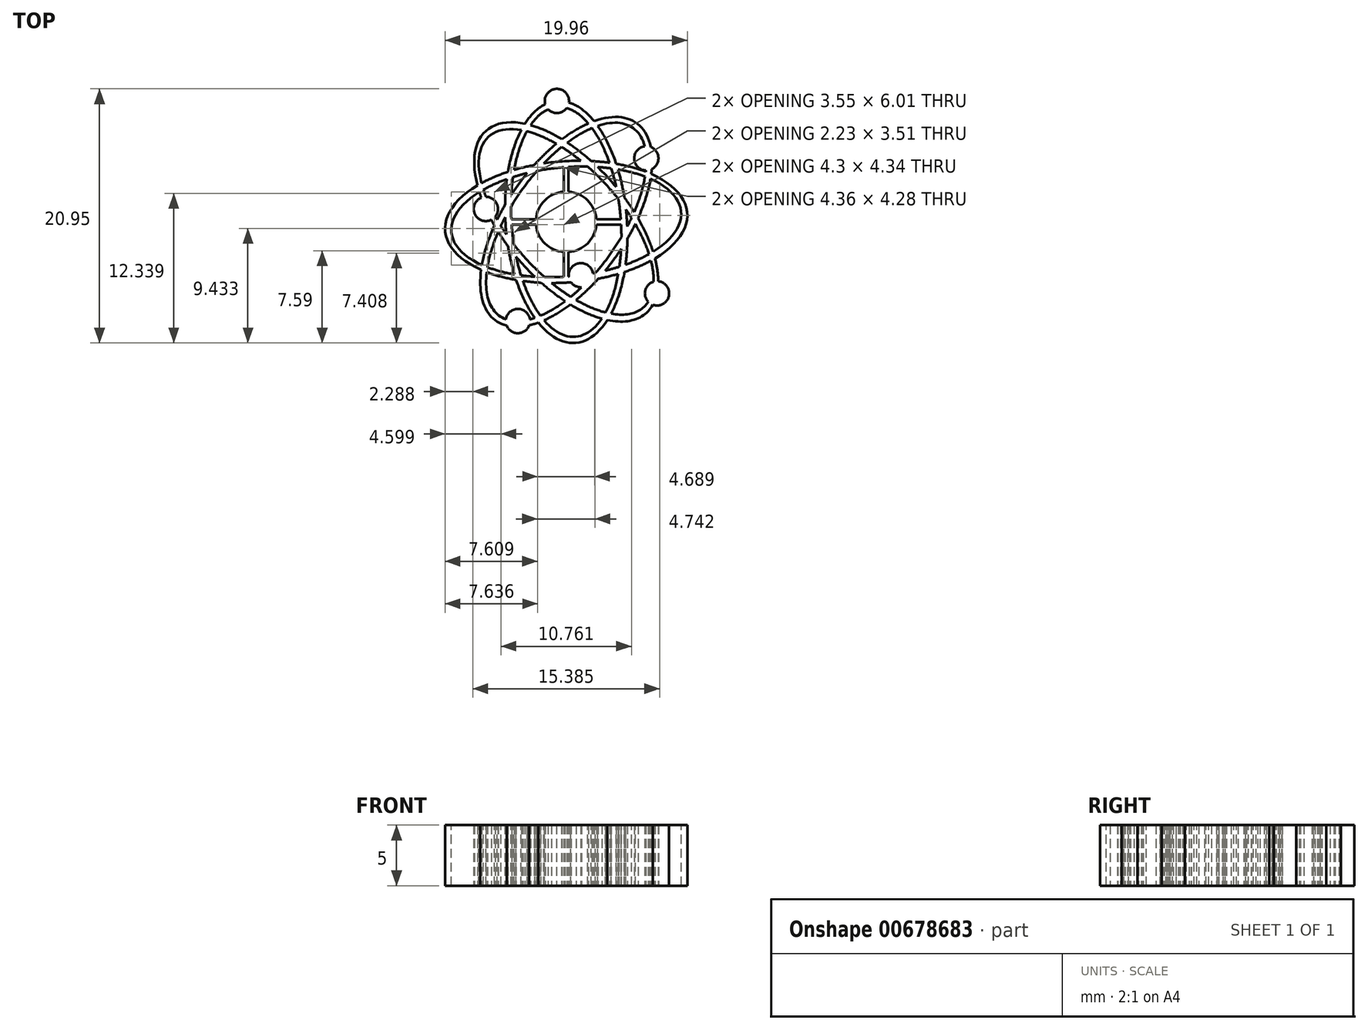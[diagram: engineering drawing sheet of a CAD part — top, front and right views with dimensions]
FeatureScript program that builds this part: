
annotation { "Feature Type Name" : "Feature", "Feature Type Description" : "" }
export const myFeature = defineFeature(function(context is Context, id is Id, definition is map)
    precondition{}
    {
        {
            var Q0;
            Q0=qCreatedBy(makeId("Top.planeOp"),FACE);
            var sketch = newSketch(context, id + "F0", { "sketchPlane" : qUnion([Q0])});
            skCircle(sketch, "E0", {"center": v(0, 0) * mm, "radius": 2.5 * mm});
            skEllipse(sketch, "E1", {"center": v(0, 0) * mm, "majorRadius": 10 * mm, "minorRadius": 5 * mm, "majorAxis": v(-0.66, 0.75)});
            skEllipse(sketch, "E2", {"center": v(0, 0) * mm, "majorRadius": 10 * mm, "minorRadius": 5 * mm, "majorAxis": v(0.58, 0.82)});
            skEllipse(sketch, "E3", {"center": v(0, 0) * mm, "majorRadius": 10 * mm, "minorRadius": 5 * mm, "majorAxis": v(-1, -0.07)});
            skEllipse(sketch, "E4", {"center": v(0, 0) * mm, "majorRadius": 9.5 * mm, "minorRadius": 4.5 * mm, "majorAxis": v(-0.67, 0.74)});
            skEllipse(sketch, "E5", {"center": v(0, 0) * mm, "majorRadius": 9.5 * mm, "minorRadius": 4.5 * mm, "majorAxis": v(-1, -0.09)});
            skEllipse(sketch, "E6", {"center": v(0, 0) * mm, "majorRadius": 9.5 * mm, "minorRadius": 4.5 * mm, "majorAxis": v(0.58, 0.82)});
            skEllipse(sketch, "E7", {"center": v(0, 0) * mm, "majorRadius": 10 * mm, "minorRadius": 5 * mm, "majorAxis": v(-0.08, 1)});
            skEllipse(sketch, "E8", {"center": v(0, 0) * mm, "majorRadius": 9.5 * mm, "minorRadius": 4.5 * mm, "majorAxis": v(-0.08, 1)});
            skCircle(sketch, "E9", {"center": v(-0.77, 9.97) * mm, "radius": 1 * mm});
            skCircle(sketch, "E10", {"center": v(-6.62, 1.07) * mm, "radius": 1 * mm});
            skCircle(sketch, "E11", {"center": v(6.6, 5.24) * mm, "radius": 1 * mm});
            skCircle(sketch, "E12", {"center": v(1.2, -4.4) * mm, "radius": 1 * mm});
            skCircle(sketch, "E13", {"center": v(7.48, -5.9) * mm, "radius": 1 * mm});
            skCircle(sketch, "E14", {"center": v(-3.98, -8.18) * mm, "radius": 1 * mm});
            skLineSegment(sketch, "E15.bottom", {"start": v(0.2, 4.78) * mm, "end": v(-0.2, 4.78) * mm});
            skLineSegment(sketch, "E15.top", {"start": v(0.2, -4.78) * mm, "end": v(-0.2, -4.78) * mm});
            skLineSegment(sketch, "E15.left", {"start": v(0.2, 4.78) * mm, "end": v(0.2, -4.78) * mm});
            skLineSegment(sketch, "E15.right", {"start": v(-0.2, 4.78) * mm, "end": v(-0.2, -4.78) * mm});
            skLineSegment(sketch, "E16.bottom", {"start": v(-4.84, -0.22) * mm, "end": v(4.84, -0.22) * mm});
            skLineSegment(sketch, "E16.top", {"start": v(-4.84, 0.22) * mm, "end": v(4.84, 0.22) * mm});
            skLineSegment(sketch, "E16.left", {"start": v(-4.84, -0.22) * mm, "end": v(-4.84, 0.22) * mm});
            skLineSegment(sketch, "E16.right", {"start": v(4.84, -0.22) * mm, "end": v(4.84, 0.22) * mm});
            skSolve(sketch);
        }
        {
            var Q0;
            Q0 = qSketchRegion(id + "F0", true);
            var Q1;
            {var subQ0=sQuery(id+"F0.wireOp",EDGE,"dH836gxZ-2VDt-7VUX-VpBF-xnlLIh1VEINP");var subQ1=sQuery(id+"F0.wireOp",EDGE,"E1");var subQ2=makeQuery(id+"F0.imprint","INTERSECT",VERTEX,{"disambiguationData":[OD(0.0)],"derivedFrom":[subQ1,subQ0]});Q1=makeQuery(id+"F0.imprint","IMPRINT",FACE,{"disambiguationData":[TD([[makeQuery(id+"F0.imprint","IMPRINT",EDGE,{"disambiguationData":[TD([[subQ2,-1.0]])],"derivedFrom":subQ1}),-1.0]])]});}
            var Q2;
            {var subQ0=sQuery(id+"F0.wireOp",EDGE,"dH836gxZ-2VDt-7VUX-VpBF-xnlLIh1VEINP");var subQ1=sQuery(id+"F0.wireOp",EDGE,"E1");var subQ2=makeQuery(id+"F0.imprint","INTERSECT",VERTEX,{"disambiguationData":[OD(0.0)],"derivedFrom":[subQ1,subQ0]});Q2=makeQuery(id+"F0.imprint","IMPRINT",FACE,{"disambiguationData":[TD([[makeQuery(id+"F0.imprint","IMPRINT",EDGE,{"disambiguationData":[TD([[subQ2,-1.0]])],"derivedFrom":subQ1}),1.0]])]});}
            var Q3;
            {var subQ0=sQuery(id+"F0.wireOp",EDGE,"dH836gxZ-2VDt-7VUX-VpBF-xnlLIh1VEINP");var subQ1=sQuery(id+"F0.wireOp",EDGE,"E4");var subQ2=makeQuery(id+"F0.imprint","INTERSECT",VERTEX,{"disambiguationData":[OD(0.0)],"derivedFrom":[subQ1,subQ0]});Q3=makeQuery(id+"F0.imprint","IMPRINT",FACE,{"disambiguationData":[TD([[makeQuery(id+"F0.imprint","IMPRINT",EDGE,{"disambiguationData":[TD([[subQ2,-1.0]])],"derivedFrom":subQ1}),1.0]])]});}
            var Q4;
            {var subQ0=sQuery(id+"F0.wireOp",EDGE,"E7");var subQ1=sQuery(id+"F0.wireOp",EDGE,"E3");var subQ2=makeQuery(id+"F0.imprint","INTERSECT",VERTEX,{"disambiguationData":[OD(1.0)],"derivedFrom":[subQ1,subQ0]});Q4=makeQuery(id+"F0.imprint","IMPRINT",FACE,{"disambiguationData":[TD([[makeQuery(id+"F0.imprint","IMPRINT",EDGE,{"disambiguationData":[TD([[subQ2,-1.0]])],"derivedFrom":subQ1}),1.0]])]});}
            var Q5;
            {var subQ0=sQuery(id+"F0.wireOp",EDGE,"E2");var subQ1=sQuery(id+"F0.wireOp",EDGE,"E1");var subQ2=makeQuery(id+"F0.imprint","INTERSECT",VERTEX,{"disambiguationData":[OD(2.0)],"derivedFrom":[subQ1,subQ0]});Q5=makeQuery(id+"F0.imprint","IMPRINT",FACE,{"disambiguationData":[TD([[makeQuery(id+"F0.imprint","IMPRINT",EDGE,{"disambiguationData":[TD([[subQ2,-1.0]])],"derivedFrom":subQ1}),-1.0]])]});}
            var Q6;
            {var subQ0=sQuery(id+"F0.wireOp",EDGE,"E2");var subQ1=sQuery(id+"F0.wireOp",EDGE,"E1");var subQ2=makeQuery(id+"F0.imprint","INTERSECT",VERTEX,{"disambiguationData":[OD(2.0)],"derivedFrom":[subQ1,subQ0]});Q6=makeQuery(id+"F0.imprint","IMPRINT",FACE,{"disambiguationData":[TD([[makeQuery(id+"F0.imprint","IMPRINT",EDGE,{"disambiguationData":[TD([[subQ2,-1.0]])],"derivedFrom":subQ1}),1.0]])]});}
            var Q7;
            {var subQ0=sQuery(id+"F0.wireOp",EDGE,"E6");var subQ1=sQuery(id+"F0.wireOp",EDGE,"E1");var subQ2=makeQuery(id+"F0.imprint","INTERSECT",VERTEX,{"disambiguationData":[OD(2.0)],"derivedFrom":[subQ1,subQ0]});Q7=makeQuery(id+"F0.imprint","IMPRINT",FACE,{"disambiguationData":[TD([[makeQuery(id+"F0.imprint","IMPRINT",EDGE,{"disambiguationData":[TD([[subQ2,-1.0]])],"derivedFrom":subQ1}),1.0]])]});}
            var Q8;
            {var subQ0=sQuery(id+"F0.wireOp",EDGE,"E7");var subQ1=sQuery(id+"F0.wireOp",EDGE,"E1");var subQ2=makeQuery(id+"F0.imprint","INTERSECT",VERTEX,{"disambiguationData":[OD(3.0)],"derivedFrom":[subQ1,subQ0]});Q8=makeQuery(id+"F0.imprint","IMPRINT",FACE,{"disambiguationData":[TD([[makeQuery(id+"F0.imprint","IMPRINT",EDGE,{"disambiguationData":[TD([[subQ2,-1.0]])],"derivedFrom":subQ1}),1.0]])]});}
            var Q9;
            {var subQ0=sQuery(id+"F0.wireOp",EDGE,"E7");var subQ1=sQuery(id+"F0.wireOp",EDGE,"E4");var subQ2=makeQuery(id+"F0.imprint","INTERSECT",VERTEX,{"disambiguationData":[OD(2.0)],"derivedFrom":[subQ1,subQ0]});Q9=makeQuery(id+"F0.imprint","IMPRINT",FACE,{"disambiguationData":[TD([[makeQuery(id+"F0.imprint","IMPRINT",EDGE,{"disambiguationData":[TD([[subQ2,-1.0]])],"derivedFrom":subQ1}),1.0]])]});}
            var Q10;
            Q10=makeQuery(id+"F0.imprint","IMPRINT",FACE,{"disambiguationData":[TD([[makeQuery(id+"F0.imprint","IMPRINT",EDGE,{"derivedFrom":sQuery(id+"F0.wireOp",EDGE,"E0")}),1.0]])]});
            var Q11;
            {var subQ0=sQuery(id+"F0.wireOp",EDGE,"E8");var subQ1=sQuery(id+"F0.wireOp",EDGE,"E1");var subQ2=makeQuery(id+"F0.imprint","INTERSECT",VERTEX,{"disambiguationData":[OD(2.0)],"derivedFrom":[subQ1,subQ0]});Q11=makeQuery(id+"F0.imprint","IMPRINT",FACE,{"disambiguationData":[TD([[makeQuery(id+"F0.imprint","IMPRINT",EDGE,{"disambiguationData":[TD([[subQ2,-1.0]])],"derivedFrom":subQ1}),1.0]])]});}
            var Q12;
            {var subQ0=sQuery(id+"F0.wireOp",EDGE,"E6");var subQ1=sQuery(id+"F0.wireOp",EDGE,"E3");var subQ2=makeQuery(id+"F0.imprint","INTERSECT",VERTEX,{"disambiguationData":[OD(2.0)],"derivedFrom":[subQ1,subQ0]});Q12=makeQuery(id+"F0.imprint","IMPRINT",FACE,{"disambiguationData":[TD([[makeQuery(id+"F0.imprint","IMPRINT",EDGE,{"disambiguationData":[TD([[subQ2,-1.0]])],"derivedFrom":subQ1}),1.0]])]});}
            var Q13;
            {var subQ0=sQuery(id+"F0.wireOp",EDGE,"E5");var subQ1=sQuery(id+"F0.wireOp",EDGE,"E1");var subQ2=makeQuery(id+"F0.imprint","INTERSECT",VERTEX,{"disambiguationData":[OD(3.0)],"derivedFrom":[subQ1,subQ0]});Q13=makeQuery(id+"F0.imprint","IMPRINT",FACE,{"disambiguationData":[TD([[makeQuery(id+"F0.imprint","IMPRINT",EDGE,{"disambiguationData":[TD([[subQ2,-1.0]])],"derivedFrom":subQ1}),-1.0]])]});}
            var Q14;
            {var subQ0=sQuery(id+"F0.wireOp",EDGE,"E11");var subQ1=sQuery(id+"F0.wireOp",EDGE,"E6");var subQ2=makeQuery(id+"F0.imprint","INTERSECT",VERTEX,{"disambiguationData":[OD(0.0)],"derivedFrom":[subQ1,subQ0]});Q14=makeQuery(id+"F0.imprint","IMPRINT",FACE,{"disambiguationData":[TD([[makeQuery(id+"F0.imprint","IMPRINT",EDGE,{"disambiguationData":[TD([[subQ2,-1.0]])],"derivedFrom":subQ1}),1.0]])]});}
            var Q15;
            {var subQ0=sQuery(id+"F0.wireOp",EDGE,"E5");var subQ1=sQuery(id+"F0.wireOp",EDGE,"E1");var subQ2=makeQuery(id+"F0.imprint","INTERSECT",VERTEX,{"disambiguationData":[OD(3.0)],"derivedFrom":[subQ1,subQ0]});Q15=makeQuery(id+"F0.imprint","IMPRINT",FACE,{"disambiguationData":[TD([[makeQuery(id+"F0.imprint","IMPRINT",EDGE,{"disambiguationData":[TD([[subQ2,-1.0]])],"derivedFrom":subQ1}),1.0]])]});}
            var Q16;
            {var subQ0=sQuery(id+"F0.wireOp",EDGE,"E3");var subQ1=sQuery(id+"F0.wireOp",EDGE,"E1");var subQ2=makeQuery(id+"F0.imprint","INTERSECT",VERTEX,{"disambiguationData":[OD(3.0)],"derivedFrom":[subQ1,subQ0]});Q16=makeQuery(id+"F0.imprint","IMPRINT",FACE,{"disambiguationData":[TD([[makeQuery(id+"F0.imprint","IMPRINT",EDGE,{"disambiguationData":[TD([[subQ2,-1.0]])],"derivedFrom":subQ1}),1.0]])]});}
            var Q17;
            {var subQ0=sQuery(id+"F0.wireOp",EDGE,"E7");var subQ1=sQuery(id+"F0.wireOp",EDGE,"E1");var subQ2=makeQuery(id+"F0.imprint","INTERSECT",VERTEX,{"disambiguationData":[OD(3.0)],"derivedFrom":[subQ1,subQ0]});Q17=makeQuery(id+"F0.imprint","IMPRINT",FACE,{"disambiguationData":[TD([[makeQuery(id+"F0.imprint","IMPRINT",EDGE,{"disambiguationData":[TD([[subQ2,-1.0]])],"derivedFrom":subQ1}),-1.0]])]});}
            var Q18;
            {var subQ0=sQuery(id+"F0.wireOp",EDGE,"E6");var subQ1=sQuery(id+"F0.wireOp",EDGE,"E1");var subQ2=makeQuery(id+"F0.imprint","INTERSECT",VERTEX,{"disambiguationData":[OD(3.0)],"derivedFrom":[subQ1,subQ0]});Q18=makeQuery(id+"F0.imprint","IMPRINT",FACE,{"disambiguationData":[TD([[makeQuery(id+"F0.imprint","IMPRINT",EDGE,{"disambiguationData":[TD([[subQ2,-1.0]])],"derivedFrom":subQ1}),1.0]])]});}
            var Q19;
            {var subQ0=sQuery(id+"F0.wireOp",EDGE,"E6");var subQ1=sQuery(id+"F0.wireOp",EDGE,"E1");var subQ2=makeQuery(id+"F0.imprint","INTERSECT",VERTEX,{"disambiguationData":[OD(3.0)],"derivedFrom":[subQ1,subQ0]});Q19=makeQuery(id+"F0.imprint","IMPRINT",FACE,{"disambiguationData":[TD([[makeQuery(id+"F0.imprint","IMPRINT",EDGE,{"disambiguationData":[TD([[subQ2,-1.0]])],"derivedFrom":subQ1}),-1.0]])]});}
            var Q20;
            {var subQ0=sQuery(id+"F0.wireOp",EDGE,"E7");var subQ1=sQuery(id+"F0.wireOp",EDGE,"E3");var subQ2=makeQuery(id+"F0.imprint","INTERSECT",VERTEX,{"disambiguationData":[OD(2.0)],"derivedFrom":[subQ1,subQ0]});Q20=makeQuery(id+"F0.imprint","IMPRINT",FACE,{"disambiguationData":[TD([[makeQuery(id+"F0.imprint","IMPRINT",EDGE,{"disambiguationData":[TD([[subQ2,-1.0]])],"derivedFrom":subQ1}),-1.0]])]});}
            var Q21;
            {var subQ0=sQuery(id+"F0.wireOp",EDGE,"E9");var subQ1=sQuery(id+"F0.wireOp",EDGE,"E8");var subQ2=makeQuery(id+"F0.imprint","INTERSECT",VERTEX,{"disambiguationData":[OD(0.0)],"derivedFrom":[subQ1,subQ0]});Q21=makeQuery(id+"F0.imprint","IMPRINT",FACE,{"disambiguationData":[TD([[makeQuery(id+"F0.imprint","IMPRINT",EDGE,{"disambiguationData":[TD([[subQ2,1.0]])],"derivedFrom":subQ1}),1.0]])]});}
            var Q22;
            {var subQ0=sQuery(id+"F0.wireOp",EDGE,"E2");var subQ1=sQuery(id+"F0.wireOp",EDGE,"E1");var subQ2=makeQuery(id+"F0.imprint","INTERSECT",VERTEX,{"disambiguationData":[OD(3.0)],"derivedFrom":[subQ1,subQ0]});Q22=makeQuery(id+"F0.imprint","IMPRINT",FACE,{"disambiguationData":[TD([[makeQuery(id+"F0.imprint","IMPRINT",EDGE,{"disambiguationData":[TD([[subQ2,-1.0]])],"derivedFrom":subQ1}),1.0]])]});}
            var Q23;
            {var subQ0=sQuery(id+"F0.wireOp",EDGE,"E8");var subQ1=sQuery(id+"F0.wireOp",EDGE,"E3");var subQ2=makeQuery(id+"F0.imprint","INTERSECT",VERTEX,{"disambiguationData":[OD(3.0)],"derivedFrom":[subQ1,subQ0]});Q23=makeQuery(id+"F0.imprint","IMPRINT",FACE,{"disambiguationData":[TD([[makeQuery(id+"F0.imprint","IMPRINT",EDGE,{"disambiguationData":[TD([[subQ2,-1.0]])],"derivedFrom":subQ1}),-1.0]])]});}
            var Q24;
            {var subQ0=sQuery(id+"F0.wireOp",EDGE,"E3");var subQ1=sQuery(id+"F0.wireOp",EDGE,"E2");var subQ2=makeQuery(id+"F0.imprint","INTERSECT",VERTEX,{"disambiguationData":[OD(2.0)],"derivedFrom":[subQ1,subQ0]});Q24=makeQuery(id+"F0.imprint","IMPRINT",FACE,{"disambiguationData":[TD([[makeQuery(id+"F0.imprint","IMPRINT",EDGE,{"disambiguationData":[TD([[subQ2,-1.0]])],"derivedFrom":subQ1}),-1.0]])]});}
            var Q25;
            {var subQ0=sQuery(id+"F0.wireOp",EDGE,"E8");var subQ1=sQuery(id+"F0.wireOp",EDGE,"E2");var subQ2=makeQuery(id+"F0.imprint","INTERSECT",VERTEX,{"disambiguationData":[OD(1.0)],"derivedFrom":[subQ1,subQ0]});Q25=makeQuery(id+"F0.imprint","IMPRINT",FACE,{"disambiguationData":[TD([[makeQuery(id+"F0.imprint","IMPRINT",EDGE,{"disambiguationData":[TD([[subQ2,-1.0]])],"derivedFrom":subQ1}),-1.0]])]});}
            var Q26;
            {var subQ0=sQuery(id+"F0.wireOp",EDGE,"E10");var subQ1=sQuery(id+"F0.wireOp",EDGE,"E4");var subQ2=makeQuery(id+"F0.imprint","INTERSECT",VERTEX,{"disambiguationData":[OD(0.0)],"derivedFrom":[subQ1,subQ0]});Q26=makeQuery(id+"F0.imprint","IMPRINT",FACE,{"disambiguationData":[TD([[makeQuery(id+"F0.imprint","IMPRINT",EDGE,{"disambiguationData":[TD([[subQ2,-1.0]])],"derivedFrom":subQ1}),1.0]])]});}
            var Q27;
            {var subQ0=sQuery(id+"F0.wireOp",EDGE,"E10");var subQ1=sQuery(id+"F0.wireOp",EDGE,"E1");var subQ2=makeQuery(id+"F0.imprint","INTERSECT",VERTEX,{"disambiguationData":[OD(0.0)],"derivedFrom":[subQ1,subQ0]});Q27=makeQuery(id+"F0.imprint","IMPRINT",FACE,{"disambiguationData":[TD([[makeQuery(id+"F0.imprint","IMPRINT",EDGE,{"disambiguationData":[TD([[subQ2,-1.0]])],"derivedFrom":subQ1}),1.0]])]});}
            var Q28;
            {var subQ0=sQuery(id+"F0.wireOp",EDGE,"E10");var subQ1=sQuery(id+"F0.wireOp",EDGE,"E1");var subQ2=makeQuery(id+"F0.imprint","INTERSECT",VERTEX,{"disambiguationData":[OD(0.0)],"derivedFrom":[subQ1,subQ0]});Q28=makeQuery(id+"F0.imprint","IMPRINT",FACE,{"disambiguationData":[TD([[makeQuery(id+"F0.imprint","IMPRINT",EDGE,{"disambiguationData":[TD([[subQ2,-1.0]])],"derivedFrom":subQ1}),-1.0]])]});}
            var Q29;
            {var subQ0=sQuery(id+"F0.wireOp",EDGE,"E5");var subQ1=sQuery(id+"F0.wireOp",EDGE,"E1");var subQ2=makeQuery(id+"F0.imprint","INTERSECT",VERTEX,{"disambiguationData":[OD(0.0)],"derivedFrom":[subQ1,subQ0]});Q29=makeQuery(id+"F0.imprint","IMPRINT",FACE,{"disambiguationData":[TD([[makeQuery(id+"F0.imprint","IMPRINT",EDGE,{"disambiguationData":[TD([[subQ2,-1.0]])],"derivedFrom":subQ1}),1.0]])]});}
            var Q30;
            {var subQ0=sQuery(id+"F0.wireOp",EDGE,"E8");var subQ1=sQuery(id+"F0.wireOp",EDGE,"E2");var subQ2=makeQuery(id+"F0.imprint","INTERSECT",VERTEX,{"disambiguationData":[OD(1.0)],"derivedFrom":[subQ1,subQ0]});Q30=makeQuery(id+"F0.imprint","IMPRINT",FACE,{"disambiguationData":[TD([[makeQuery(id+"F0.imprint","IMPRINT",EDGE,{"disambiguationData":[TD([[subQ2,-1.0]])],"derivedFrom":subQ1}),1.0]])]});}
            var Q31;
            {var subQ0=sQuery(id+"F0.wireOp",EDGE,"E5");var subQ1=sQuery(id+"F0.wireOp",EDGE,"E2");var subQ2=makeQuery(id+"F0.imprint","INTERSECT",VERTEX,{"disambiguationData":[OD(0.0)],"derivedFrom":[subQ1,subQ0]});Q31=makeQuery(id+"F0.imprint","IMPRINT",FACE,{"disambiguationData":[TD([[makeQuery(id+"F0.imprint","IMPRINT",EDGE,{"disambiguationData":[TD([[subQ2,-1.0]])],"derivedFrom":subQ1}),1.0]])]});}
            var Q32;
            {var subQ0=sQuery(id+"F0.wireOp",EDGE,"E2");var subQ1=sQuery(id+"F0.wireOp",EDGE,"E1");var subQ2=makeQuery(id+"F0.imprint","INTERSECT",VERTEX,{"disambiguationData":[OD(0.0)],"derivedFrom":[subQ1,subQ0]});Q32=makeQuery(id+"F0.imprint","IMPRINT",FACE,{"disambiguationData":[TD([[makeQuery(id+"F0.imprint","IMPRINT",EDGE,{"disambiguationData":[TD([[subQ2,-1.0]])],"derivedFrom":subQ1}),1.0]])]});}
            var Q33;
            {var subQ0=sQuery(id+"F0.wireOp",EDGE,"E2");var subQ1=sQuery(id+"F0.wireOp",EDGE,"E1");var subQ2=makeQuery(id+"F0.imprint","INTERSECT",VERTEX,{"disambiguationData":[OD(0.0)],"derivedFrom":[subQ1,subQ0]});Q33=makeQuery(id+"F0.imprint","IMPRINT",FACE,{"disambiguationData":[TD([[makeQuery(id+"F0.imprint","IMPRINT",EDGE,{"disambiguationData":[TD([[subQ2,-1.0]])],"derivedFrom":subQ1}),-1.0]])]});}
            var Q34;
            {var subQ0=sQuery(id+"F0.wireOp",EDGE,"E6");var subQ1=sQuery(id+"F0.wireOp",EDGE,"E1");var subQ2=makeQuery(id+"F0.imprint","INTERSECT",VERTEX,{"disambiguationData":[OD(0.0)],"derivedFrom":[subQ1,subQ0]});Q34=makeQuery(id+"F0.imprint","IMPRINT",FACE,{"disambiguationData":[TD([[makeQuery(id+"F0.imprint","IMPRINT",EDGE,{"disambiguationData":[TD([[subQ2,-1.0]])],"derivedFrom":subQ1}),1.0]])]});}
            var Q35;
            {var subQ0=sQuery(id+"F0.wireOp",EDGE,"E7");var subQ1=sQuery(id+"F0.wireOp",EDGE,"E1");var subQ2=makeQuery(id+"F0.imprint","INTERSECT",VERTEX,{"disambiguationData":[OD(2.0)],"derivedFrom":[subQ1,subQ0]});Q35=makeQuery(id+"F0.imprint","IMPRINT",FACE,{"disambiguationData":[TD([[makeQuery(id+"F0.imprint","IMPRINT",EDGE,{"disambiguationData":[TD([[subQ2,-1.0]])],"derivedFrom":subQ1}),1.0]])]});}
            var Q36;
            {var subQ0=sQuery(id+"F0.wireOp",EDGE,"E7");var subQ1=sQuery(id+"F0.wireOp",EDGE,"E4");var subQ2=makeQuery(id+"F0.imprint","INTERSECT",VERTEX,{"disambiguationData":[OD(0.0)],"derivedFrom":[subQ1,subQ0]});Q36=makeQuery(id+"F0.imprint","IMPRINT",FACE,{"disambiguationData":[TD([[makeQuery(id+"F0.imprint","IMPRINT",EDGE,{"disambiguationData":[TD([[subQ2,-1.0]])],"derivedFrom":subQ1}),1.0]])]});}
            var Q37;
            {var subQ0=sQuery(id+"F0.wireOp",EDGE,"E7");var subQ1=sQuery(id+"F0.wireOp",EDGE,"E3");var subQ2=makeQuery(id+"F0.imprint","INTERSECT",VERTEX,{"disambiguationData":[OD(2.0)],"derivedFrom":[subQ1,subQ0]});Q37=makeQuery(id+"F0.imprint","IMPRINT",FACE,{"disambiguationData":[TD([[makeQuery(id+"F0.imprint","IMPRINT",EDGE,{"disambiguationData":[TD([[subQ2,-1.0]])],"derivedFrom":subQ1}),1.0]])]});}
            var Q38;
            {var subQ0=sQuery(id+"F0.wireOp",EDGE,"E4");var subQ1=sQuery(id+"F0.wireOp",EDGE,"E3");var subQ2=makeQuery(id+"F0.imprint","INTERSECT",VERTEX,{"disambiguationData":[OD(2.0)],"derivedFrom":[subQ1,subQ0]});Q38=makeQuery(id+"F0.imprint","IMPRINT",FACE,{"disambiguationData":[TD([[makeQuery(id+"F0.imprint","IMPRINT",EDGE,{"disambiguationData":[TD([[subQ2,-1.0]])],"derivedFrom":subQ1}),1.0]])]});}
            var Q39;
            {var subQ0=sQuery(id+"F0.wireOp",EDGE,"E4");var subQ1=sQuery(id+"F0.wireOp",EDGE,"E2");var subQ2=makeQuery(id+"F0.imprint","INTERSECT",VERTEX,{"disambiguationData":[OD(0.0)],"derivedFrom":[subQ1,subQ0]});Q39=makeQuery(id+"F0.imprint","IMPRINT",FACE,{"disambiguationData":[TD([[makeQuery(id+"F0.imprint","IMPRINT",EDGE,{"disambiguationData":[TD([[subQ2,-1.0]])],"derivedFrom":subQ1}),1.0]])]});}
            var Q40;
            {var subQ0=sQuery(id+"F0.wireOp",EDGE,"E3");var subQ1=sQuery(id+"F0.wireOp",EDGE,"E2");var subQ2=makeQuery(id+"F0.imprint","INTERSECT",VERTEX,{"disambiguationData":[OD(2.0)],"derivedFrom":[subQ1,subQ0]});Q40=makeQuery(id+"F0.imprint","IMPRINT",FACE,{"disambiguationData":[TD([[makeQuery(id+"F0.imprint","IMPRINT",EDGE,{"disambiguationData":[TD([[subQ2,-1.0]])],"derivedFrom":subQ1}),1.0]])]});}
            var Q41;
            {var subQ0=sQuery(id+"F0.wireOp",EDGE,"E7");var subQ1=sQuery(id+"F0.wireOp",EDGE,"E3");var subQ2=makeQuery(id+"F0.imprint","INTERSECT",VERTEX,{"disambiguationData":[OD(3.0)],"derivedFrom":[subQ1,subQ0]});Q41=makeQuery(id+"F0.imprint","IMPRINT",FACE,{"disambiguationData":[TD([[makeQuery(id+"F0.imprint","IMPRINT",EDGE,{"disambiguationData":[TD([[subQ2,-1.0]])],"derivedFrom":subQ1}),1.0]])]});}
            var Q42;
            {var subQ0=sQuery(id+"F0.wireOp",EDGE,"E7");var subQ1=sQuery(id+"F0.wireOp",EDGE,"E1");var subQ2=makeQuery(id+"F0.imprint","INTERSECT",VERTEX,{"disambiguationData":[OD(2.0)],"derivedFrom":[subQ1,subQ0]});Q42=makeQuery(id+"F0.imprint","IMPRINT",FACE,{"disambiguationData":[TD([[makeQuery(id+"F0.imprint","IMPRINT",EDGE,{"disambiguationData":[TD([[subQ2,-1.0]])],"derivedFrom":subQ1}),-1.0]])]});}
            var Q43;
            {var subQ0=sQuery(id+"F0.wireOp",EDGE,"E12");var subQ1=sQuery(id+"F0.wireOp",EDGE,"E5");var subQ2=makeQuery(id+"F0.imprint","INTERSECT",VERTEX,{"disambiguationData":[OD(0.0)],"derivedFrom":[subQ1,subQ0]});Q43=makeQuery(id+"F0.imprint","IMPRINT",FACE,{"disambiguationData":[TD([[makeQuery(id+"F0.imprint","IMPRINT",EDGE,{"disambiguationData":[TD([[subQ2,-1.0]])],"derivedFrom":subQ1}),1.0]])]});}
            var Q44;
            {var subQ0=sQuery(id+"F0.wireOp",EDGE,"E5");var subQ1=sQuery(id+"F0.wireOp",EDGE,"E1");var subQ2=makeQuery(id+"F0.imprint","INTERSECT",VERTEX,{"disambiguationData":[OD(2.0)],"derivedFrom":[subQ1,subQ0]});Q44=makeQuery(id+"F0.imprint","IMPRINT",FACE,{"disambiguationData":[TD([[makeQuery(id+"F0.imprint","IMPRINT",EDGE,{"disambiguationData":[TD([[subQ2,-1.0]])],"derivedFrom":subQ1}),1.0]])]});}
            var Q45;
            {var subQ0=sQuery(id+"F0.wireOp",EDGE,"dH836gxZ-2VDt-7VUX-VpBF-xnlLIh1VEINP");var subQ1=sQuery(id+"F0.wireOp",EDGE,"E1");var subQ2=makeQuery(id+"F0.imprint","INTERSECT",VERTEX,{"disambiguationData":[OD(1.0)],"derivedFrom":[subQ1,subQ0]});Q45=makeQuery(id+"F0.imprint","IMPRINT",FACE,{"disambiguationData":[TD([[makeQuery(id+"F0.imprint","IMPRINT",EDGE,{"disambiguationData":[TD([[subQ2,-1.0]])],"derivedFrom":subQ1}),1.0]])]});}
            var Q46;
            {var subQ0=sQuery(id+"F0.wireOp",EDGE,"E8");var subQ1=sQuery(id+"F0.wireOp",EDGE,"E2");var subQ2=makeQuery(id+"F0.imprint","INTERSECT",VERTEX,{"disambiguationData":[OD(3.0)],"derivedFrom":[subQ1,subQ0]});Q46=makeQuery(id+"F0.imprint","IMPRINT",FACE,{"disambiguationData":[TD([[makeQuery(id+"F0.imprint","IMPRINT",EDGE,{"disambiguationData":[TD([[subQ2,-1.0]])],"derivedFrom":subQ1}),-1.0]])]});}
            var Q47;
            {var subQ0=sQuery(id+"F0.wireOp",EDGE,"E8");var subQ1=sQuery(id+"F0.wireOp",EDGE,"E3");var subQ2=makeQuery(id+"F0.imprint","INTERSECT",VERTEX,{"disambiguationData":[OD(1.0)],"derivedFrom":[subQ1,subQ0]});Q47=makeQuery(id+"F0.imprint","IMPRINT",FACE,{"disambiguationData":[TD([[makeQuery(id+"F0.imprint","IMPRINT",EDGE,{"disambiguationData":[TD([[subQ2,-1.0]])],"derivedFrom":subQ1}),-1.0]])]});}
            var Q48;
            {var subQ0=sQuery(id+"F0.wireOp",EDGE,"E2");var subQ1=sQuery(id+"F0.wireOp",EDGE,"E1");var subQ2=makeQuery(id+"F0.imprint","INTERSECT",VERTEX,{"disambiguationData":[OD(1.0)],"derivedFrom":[subQ1,subQ0]});Q48=makeQuery(id+"F0.imprint","IMPRINT",FACE,{"disambiguationData":[TD([[makeQuery(id+"F0.imprint","IMPRINT",EDGE,{"disambiguationData":[TD([[subQ2,-1.0]])],"derivedFrom":subQ1}),1.0]])]});}
            var Q49;
            {var subQ0=sQuery(id+"F0.wireOp",EDGE,"E6");var subQ1=sQuery(id+"F0.wireOp",EDGE,"E1");var subQ2=makeQuery(id+"F0.imprint","INTERSECT",VERTEX,{"disambiguationData":[OD(1.0)],"derivedFrom":[subQ1,subQ0]});Q49=makeQuery(id+"F0.imprint","IMPRINT",FACE,{"disambiguationData":[TD([[makeQuery(id+"F0.imprint","IMPRINT",EDGE,{"disambiguationData":[TD([[subQ2,-1.0]])],"derivedFrom":subQ1}),1.0]])]});}
            var Q50;
            {var subQ0=sQuery(id+"F0.wireOp",EDGE,"E3");var subQ1=sQuery(id+"F0.wireOp",EDGE,"E1");var subQ2=makeQuery(id+"F0.imprint","INTERSECT",VERTEX,{"disambiguationData":[OD(2.0)],"derivedFrom":[subQ1,subQ0]});Q50=makeQuery(id+"F0.imprint","IMPRINT",FACE,{"disambiguationData":[TD([[makeQuery(id+"F0.imprint","IMPRINT",EDGE,{"disambiguationData":[TD([[subQ2,-1.0]])],"derivedFrom":subQ1}),1.0]])]});}
            var Q51;
            {var subQ0=sQuery(id+"F0.wireOp",EDGE,"E6");var subQ1=sQuery(id+"F0.wireOp",EDGE,"E1");var subQ2=makeQuery(id+"F0.imprint","INTERSECT",VERTEX,{"disambiguationData":[OD(1.0)],"derivedFrom":[subQ1,subQ0]});Q51=makeQuery(id+"F0.imprint","IMPRINT",FACE,{"disambiguationData":[TD([[makeQuery(id+"F0.imprint","IMPRINT",EDGE,{"disambiguationData":[TD([[subQ2,-1.0]])],"derivedFrom":subQ1}),-1.0]])]});}
            var Q52;
            {var subQ0=sQuery(id+"F0.wireOp",EDGE,"E7");var subQ1=sQuery(id+"F0.wireOp",EDGE,"E3");var subQ2=makeQuery(id+"F0.imprint","INTERSECT",VERTEX,{"disambiguationData":[OD(0.0)],"derivedFrom":[subQ1,subQ0]});Q52=makeQuery(id+"F0.imprint","IMPRINT",FACE,{"disambiguationData":[TD([[makeQuery(id+"F0.imprint","IMPRINT",EDGE,{"disambiguationData":[TD([[subQ2,-1.0]])],"derivedFrom":subQ1}),-1.0]])]});}
            var Q53;
            {var subQ0=sQuery(id+"F0.wireOp",EDGE,"E7");var subQ1=sQuery(id+"F0.wireOp",EDGE,"E3");var subQ2=makeQuery(id+"F0.imprint","INTERSECT",VERTEX,{"disambiguationData":[OD(0.0)],"derivedFrom":[subQ1,subQ0]});Q53=makeQuery(id+"F0.imprint","IMPRINT",FACE,{"disambiguationData":[TD([[makeQuery(id+"F0.imprint","IMPRINT",EDGE,{"disambiguationData":[TD([[subQ2,-1.0]])],"derivedFrom":subQ1}),1.0]])]});}
            var Q54;
            {var subQ0=sQuery(id+"F0.wireOp",EDGE,"E6");var subQ1=sQuery(id+"F0.wireOp",EDGE,"E3");var subQ2=makeQuery(id+"F0.imprint","INTERSECT",VERTEX,{"disambiguationData":[OD(0.0)],"derivedFrom":[subQ1,subQ0]});Q54=makeQuery(id+"F0.imprint","IMPRINT",FACE,{"disambiguationData":[TD([[makeQuery(id+"F0.imprint","IMPRINT",EDGE,{"disambiguationData":[TD([[subQ2,-1.0]])],"derivedFrom":subQ1}),1.0]])]});}
            var Q55;
            {var subQ0=sQuery(id+"F0.wireOp",EDGE,"E5");var subQ1=sQuery(id+"F0.wireOp",EDGE,"E1");var subQ2=makeQuery(id+"F0.imprint","INTERSECT",VERTEX,{"disambiguationData":[OD(1.0)],"derivedFrom":[subQ1,subQ0]});Q55=makeQuery(id+"F0.imprint","IMPRINT",FACE,{"disambiguationData":[TD([[makeQuery(id+"F0.imprint","IMPRINT",EDGE,{"disambiguationData":[TD([[subQ2,-1.0]])],"derivedFrom":subQ1}),-1.0]])]});}
            var Q56;
            {var subQ0=sQuery(id+"F0.wireOp",EDGE,"E5");var subQ1=sQuery(id+"F0.wireOp",EDGE,"E1");var subQ2=makeQuery(id+"F0.imprint","INTERSECT",VERTEX,{"disambiguationData":[OD(1.0)],"derivedFrom":[subQ1,subQ0]});Q56=makeQuery(id+"F0.imprint","IMPRINT",FACE,{"disambiguationData":[TD([[makeQuery(id+"F0.imprint","IMPRINT",EDGE,{"disambiguationData":[TD([[subQ2,-1.0]])],"derivedFrom":subQ1}),1.0]])]});}
            var Q57;
            {var subQ0=sQuery(id+"F0.wireOp",EDGE,"E4");var subQ1=sQuery(id+"F0.wireOp",EDGE,"E3");var subQ2=makeQuery(id+"F0.imprint","INTERSECT",VERTEX,{"disambiguationData":[OD(0.0)],"derivedFrom":[subQ1,subQ0]});Q57=makeQuery(id+"F0.imprint","IMPRINT",FACE,{"disambiguationData":[TD([[makeQuery(id+"F0.imprint","IMPRINT",EDGE,{"disambiguationData":[TD([[subQ2,-1.0]])],"derivedFrom":subQ1}),1.0]])]});}
            var Q58;
            {var subQ0=sQuery(id+"F0.wireOp",EDGE,"E12");var subQ1=sQuery(id+"F0.wireOp",EDGE,"E3");var subQ2=makeQuery(id+"F0.imprint","INTERSECT",VERTEX,{"disambiguationData":[OD(0.0)],"derivedFrom":[subQ1,subQ0]});Q58=makeQuery(id+"F0.imprint","IMPRINT",FACE,{"disambiguationData":[TD([[makeQuery(id+"F0.imprint","IMPRINT",EDGE,{"disambiguationData":[TD([[subQ2,-1.0]])],"derivedFrom":subQ1}),1.0]])]});}
            var Q59;
            {var subQ0=sQuery(id+"F0.wireOp",EDGE,"E12");var subQ1=sQuery(id+"F0.wireOp",EDGE,"E3");var subQ2=makeQuery(id+"F0.imprint","INTERSECT",VERTEX,{"disambiguationData":[OD(0.0)],"derivedFrom":[subQ1,subQ0]});Q59=makeQuery(id+"F0.imprint","IMPRINT",FACE,{"disambiguationData":[TD([[makeQuery(id+"F0.imprint","IMPRINT",EDGE,{"disambiguationData":[TD([[subQ2,-1.0]])],"derivedFrom":subQ1}),-1.0]])]});}
            var Q60;
            {var subQ0=sQuery(id+"F0.wireOp",EDGE,"E4");var subQ1=sQuery(id+"F0.wireOp",EDGE,"E2");var subQ2=makeQuery(id+"F0.imprint","INTERSECT",VERTEX,{"disambiguationData":[OD(2.0)],"derivedFrom":[subQ1,subQ0]});Q60=makeQuery(id+"F0.imprint","IMPRINT",FACE,{"disambiguationData":[TD([[makeQuery(id+"F0.imprint","IMPRINT",EDGE,{"disambiguationData":[TD([[subQ2,-1.0]])],"derivedFrom":subQ1}),1.0]])]});}
            var Q61;
            {var subQ0=sQuery(id+"F0.wireOp",EDGE,"E5");var subQ1=sQuery(id+"F0.wireOp",EDGE,"E2");var subQ2=makeQuery(id+"F0.imprint","INTERSECT",VERTEX,{"disambiguationData":[OD(2.0)],"derivedFrom":[subQ1,subQ0]});Q61=makeQuery(id+"F0.imprint","IMPRINT",FACE,{"disambiguationData":[TD([[makeQuery(id+"F0.imprint","IMPRINT",EDGE,{"disambiguationData":[TD([[subQ2,-1.0]])],"derivedFrom":subQ1}),1.0]])]});}
            var Q62;
            {var subQ5=sQuery(id+"F0.wireOp",EDGE,"E2");var subQ7=sQuery(id+"F0.wireOp",EDGE,"E3");var subQ8=makeQuery(id+"F0.imprint","INTERSECT",VERTEX,{"disambiguationData":[OD(3.0)],"derivedFrom":[subQ5,subQ7]});Q62=makeQuery(id+"F0.imprint","IMPRINT",FACE,{"disambiguationData":[TD([[makeQuery(id+"F0.imprint","IMPRINT",EDGE,{"disambiguationData":[TD([[subQ8,-1.0]])],"derivedFrom":subQ5}),1.0]])]});}
            var Q63;
            {var subQ0=sQuery(id+"F0.wireOp",EDGE,"E3");var subQ1=sQuery(id+"F0.wireOp",EDGE,"E2");var subQ2=makeQuery(id+"F0.imprint","INTERSECT",VERTEX,{"disambiguationData":[OD(3.0)],"derivedFrom":[subQ1,subQ0]});Q63=makeQuery(id+"F0.imprint","IMPRINT",FACE,{"disambiguationData":[TD([[makeQuery(id+"F0.imprint","IMPRINT",EDGE,{"disambiguationData":[TD([[subQ2,-1.0]])],"derivedFrom":subQ1}),-1.0]])]});}
            var Q64;
            {var subQ0=sQuery(id+"F0.wireOp",EDGE,"E8");var subQ1=sQuery(id+"F0.wireOp",EDGE,"E3");var subQ2=makeQuery(id+"F0.imprint","INTERSECT",VERTEX,{"disambiguationData":[OD(1.0)],"derivedFrom":[subQ1,subQ0]});Q64=makeQuery(id+"F0.imprint","IMPRINT",FACE,{"disambiguationData":[TD([[makeQuery(id+"F0.imprint","IMPRINT",EDGE,{"disambiguationData":[TD([[subQ2,-1.0]])],"derivedFrom":subQ1}),1.0]])]});}
            var Q65;
            {var subQ0=sQuery(id+"F0.wireOp",EDGE,"E8");var subQ1=sQuery(id+"F0.wireOp",EDGE,"E2");var subQ2=makeQuery(id+"F0.imprint","INTERSECT",VERTEX,{"disambiguationData":[OD(3.0)],"derivedFrom":[subQ1,subQ0]});Q65=makeQuery(id+"F0.imprint","IMPRINT",FACE,{"disambiguationData":[TD([[makeQuery(id+"F0.imprint","IMPRINT",EDGE,{"disambiguationData":[TD([[subQ2,-1.0]])],"derivedFrom":subQ1}),1.0]])]});}
            var Q66;
            {var subQ0=sQuery(id+"F0.wireOp",EDGE,"FGsoe8se-pEv1-pscI-4Cfm-XyZzlzuOyecf");var subQ1=sQuery(id+"F0.wireOp",EDGE,"E6");var subQ2=makeQuery(id+"F0.imprint","INTERSECT",VERTEX,{"disambiguationData":[OD(0.0)],"derivedFrom":[subQ1,subQ0]});Q66=makeQuery(id+"F0.imprint","IMPRINT",FACE,{"disambiguationData":[TD([[makeQuery(id+"F0.imprint","IMPRINT",EDGE,{"disambiguationData":[TD([[subQ2,-1.0]])],"derivedFrom":subQ1}),1.0]])]});}
            var Q67;
            {var subQ0=sQuery(id+"F0.wireOp",EDGE,"E8");var subQ1=sQuery(id+"F0.wireOp",EDGE,"E1");var subQ2=makeQuery(id+"F0.imprint","INTERSECT",VERTEX,{"disambiguationData":[OD(0.0)],"derivedFrom":[subQ1,subQ0]});Q67=makeQuery(id+"F0.imprint","IMPRINT",FACE,{"disambiguationData":[TD([[makeQuery(id+"F0.imprint","IMPRINT",EDGE,{"disambiguationData":[TD([[subQ2,-1.0]])],"derivedFrom":subQ1}),1.0]])]});}
            var Q68;
            {var subQ0=sQuery(id+"F0.wireOp",EDGE,"E7");var subQ1=sQuery(id+"F0.wireOp",EDGE,"E2");var subQ2=makeQuery(id+"F0.imprint","INTERSECT",VERTEX,{"disambiguationData":[OD(2.0)],"derivedFrom":[subQ1,subQ0]});Q68=makeQuery(id+"F0.imprint","IMPRINT",FACE,{"disambiguationData":[TD([[makeQuery(id+"F0.imprint","IMPRINT",EDGE,{"disambiguationData":[TD([[subQ2,-1.0]])],"derivedFrom":subQ1}),1.0]])]});}
            var Q69;
            {var subQ0=sQuery(id+"F0.wireOp",EDGE,"E10");var subQ1=sQuery(id+"F0.wireOp",EDGE,"E1");var subQ2=makeQuery(id+"F0.imprint","INTERSECT",VERTEX,{"disambiguationData":[OD(1.0)],"derivedFrom":[subQ1,subQ0]});Q69=makeQuery(id+"F0.imprint","IMPRINT",FACE,{"disambiguationData":[TD([[makeQuery(id+"F0.imprint","IMPRINT",EDGE,{"disambiguationData":[TD([[subQ2,-1.0]])],"derivedFrom":subQ1}),1.0]])]});}
            var Q70;
            {var subQ0=sQuery(id+"F0.wireOp",EDGE,"E8");var subQ1=sQuery(id+"F0.wireOp",EDGE,"E3");var subQ2=makeQuery(id+"F0.imprint","INTERSECT",VERTEX,{"disambiguationData":[OD(3.0)],"derivedFrom":[subQ1,subQ0]});Q70=makeQuery(id+"F0.imprint","IMPRINT",FACE,{"disambiguationData":[TD([[makeQuery(id+"F0.imprint","IMPRINT",EDGE,{"disambiguationData":[TD([[subQ2,-1.0]])],"derivedFrom":subQ1}),1.0]])]});}
            var Q71;
            {var subQ0=sQuery(id+"F0.wireOp",EDGE,"E7");var subQ1=sQuery(id+"F0.wireOp",EDGE,"E2");var subQ2=makeQuery(id+"F0.imprint","INTERSECT",VERTEX,{"disambiguationData":[OD(3.0)],"derivedFrom":[subQ1,subQ0]});Q71=makeQuery(id+"F0.imprint","IMPRINT",FACE,{"disambiguationData":[TD([[makeQuery(id+"F0.imprint","IMPRINT",EDGE,{"disambiguationData":[TD([[subQ2,-1.0]])],"derivedFrom":subQ1}),1.0]])]});}
            var Q72;
            {var subQ0=sQuery(id+"F0.wireOp",EDGE,"E6");var subQ1=sQuery(id+"F0.wireOp",EDGE,"E3");var subQ2=makeQuery(id+"F0.imprint","INTERSECT",VERTEX,{"disambiguationData":[OD(1.0)],"derivedFrom":[subQ1,subQ0]});Q72=makeQuery(id+"F0.imprint","IMPRINT",FACE,{"disambiguationData":[TD([[makeQuery(id+"F0.imprint","IMPRINT",EDGE,{"disambiguationData":[TD([[subQ2,-1.0]])],"derivedFrom":subQ1}),-1.0]])]});}
            var Q73;
            {var subQ0=sQuery(id+"F0.wireOp",EDGE,"E6");var subQ1=sQuery(id+"F0.wireOp",EDGE,"E3");var subQ2=makeQuery(id+"F0.imprint","INTERSECT",VERTEX,{"disambiguationData":[OD(1.0)],"derivedFrom":[subQ1,subQ0]});Q73=makeQuery(id+"F0.imprint","IMPRINT",FACE,{"disambiguationData":[TD([[makeQuery(id+"F0.imprint","IMPRINT",EDGE,{"disambiguationData":[TD([[subQ2,-1.0]])],"derivedFrom":subQ1}),1.0]])]});}
            var Q74;
            {var subQ0=sQuery(id+"F0.wireOp",EDGE,"E12");var subQ1=sQuery(id+"F0.wireOp",EDGE,"E5");var subQ2=makeQuery(id+"F0.imprint","INTERSECT",VERTEX,{"disambiguationData":[OD(1.0)],"derivedFrom":[subQ1,subQ0]});Q74=makeQuery(id+"F0.imprint","IMPRINT",FACE,{"disambiguationData":[TD([[makeQuery(id+"F0.imprint","IMPRINT",EDGE,{"disambiguationData":[TD([[subQ2,-1.0]])],"derivedFrom":subQ1}),-1.0]])]});}
            var Q75;
            {var subQ0=sQuery(id+"F0.wireOp",EDGE,"E14");var subQ1=sQuery(id+"F0.wireOp",EDGE,"E6");var subQ2=makeQuery(id+"F0.imprint","INTERSECT",VERTEX,{"disambiguationData":[OD(0.0)],"derivedFrom":[subQ1,subQ0]});Q75=makeQuery(id+"F0.imprint","IMPRINT",FACE,{"disambiguationData":[TD([[makeQuery(id+"F0.imprint","IMPRINT",EDGE,{"disambiguationData":[TD([[subQ2,-1.0]])],"derivedFrom":subQ1}),1.0]])]});}
            var Q76;
            {var subQ0=sQuery(id+"F0.wireOp",EDGE,"E13");var subQ1=sQuery(id+"F0.wireOp",EDGE,"E4");var subQ2=makeQuery(id+"F0.imprint","INTERSECT",VERTEX,{"disambiguationData":[OD(0.0)],"derivedFrom":[subQ1,subQ0]});Q76=makeQuery(id+"F0.imprint","IMPRINT",FACE,{"disambiguationData":[TD([[makeQuery(id+"F0.imprint","IMPRINT",EDGE,{"disambiguationData":[TD([[subQ2,-1.0]])],"derivedFrom":subQ1}),1.0]])]});}
            var Q77;
            {var subQ0=sQuery(id+"F0.wireOp",EDGE,"E15.right");var subQ1=sQuery(id+"F0.wireOp",EDGE,"E0");var subQ2=makeQuery(id+"F0.imprint","INTERSECT",VERTEX,{"disambiguationData":[OD(0.0)],"derivedFrom":[subQ1,subQ0]});Q77=makeQuery(id+"F0.imprint","IMPRINT",FACE,{"disambiguationData":[TD([[makeQuery(id+"F0.imprint","IMPRINT",EDGE,{"disambiguationData":[TD([[subQ2,1.0]])],"derivedFrom":subQ1}),-1.0]])]});}
            var Q78;
            {var subQ0=sQuery(id+"F0.wireOp",EDGE,"E15.left");var subQ1=sQuery(id+"F0.wireOp",EDGE,"E0");var subQ2=makeQuery(id+"F0.imprint","INTERSECT",VERTEX,{"disambiguationData":[OD(0.0)],"derivedFrom":[subQ1,subQ0]});Q78=makeQuery(id+"F0.imprint","IMPRINT",FACE,{"disambiguationData":[TD([[makeQuery(id+"F0.imprint","IMPRINT",EDGE,{"disambiguationData":[TD([[subQ2,1.0]])],"derivedFrom":subQ1}),1.0]])]});}
            var Q79;
            {var subQ0=sQuery(id+"F0.wireOp",EDGE,"E15.right");var subQ1=sQuery(id+"F0.wireOp",EDGE,"E0");var subQ2=makeQuery(id+"F0.imprint","INTERSECT",VERTEX,{"disambiguationData":[OD(0.0)],"derivedFrom":[subQ1,subQ0]});Q79=makeQuery(id+"F0.imprint","IMPRINT",FACE,{"disambiguationData":[TD([[makeQuery(id+"F0.imprint","IMPRINT",EDGE,{"disambiguationData":[TD([[subQ2,-1.0]])],"derivedFrom":subQ1}),1.0]])]});}
            var Q80;
            {var subQ0=sQuery(id+"F0.wireOp",EDGE,"E15.right");var subQ1=sQuery(id+"F0.wireOp",EDGE,"E0");var subQ2=makeQuery(id+"F0.imprint","INTERSECT",VERTEX,{"disambiguationData":[OD(1.0)],"derivedFrom":[subQ1,subQ0]});Q80=makeQuery(id+"F0.imprint","IMPRINT",FACE,{"disambiguationData":[TD([[makeQuery(id+"F0.imprint","IMPRINT",EDGE,{"disambiguationData":[TD([[subQ2,-1.0]])],"derivedFrom":subQ1}),-1.0]])]});}
            var Q81;
            {var subQ5=sQuery(id+"F0.wireOp",EDGE,"E15.bottom");Q81=makeQuery(id+"F0.imprint","IMPRINT",FACE,{"disambiguationData":[TD([[makeQuery(id+"F0.imprint","IMPRINT",EDGE,{"derivedFrom":subQ5}),1.0]])]});}
            var Q82;
            {var subQ5=sQuery(id+"F0.wireOp",EDGE,"E15.top");Q82=makeQuery(id+"F0.imprint","IMPRINT",FACE,{"disambiguationData":[TD([[makeQuery(id+"F0.imprint","IMPRINT",EDGE,{"derivedFrom":subQ5}),-1.0]])]});}
            var Q83;
            {var subQ0=sQuery(id+"F0.wireOp",EDGE,"E16.top");var subQ1=sQuery(id+"F0.wireOp",EDGE,"E0");var subQ2=makeQuery(id+"F0.imprint","INTERSECT",VERTEX,{"disambiguationData":[OD(1.0)],"derivedFrom":[subQ1,subQ0]});Q83=makeQuery(id+"F0.imprint","IMPRINT",FACE,{"disambiguationData":[TD([[makeQuery(id+"F0.imprint","IMPRINT",EDGE,{"disambiguationData":[TD([[subQ2,-1.0]])],"derivedFrom":subQ1}),1.0]])]});}
            var Q84;
            {var subQ0=sQuery(id+"F0.wireOp",EDGE,"E16.top");var subQ1=sQuery(id+"F0.wireOp",EDGE,"E15.left");var subQ2=makeQuery(id+"F0.imprint","INTERSECT",VERTEX,{"derivedFrom":[subQ1,subQ0]});Q84=makeQuery(id+"F0.imprint","IMPRINT",FACE,{"disambiguationData":[TD([[makeQuery(id+"F0.imprint","IMPRINT",EDGE,{"disambiguationData":[TD([[subQ2,-1.0]])],"derivedFrom":subQ1}),-1.0]])]});}
            var Q85;
            {var subQ0=sQuery(id+"F0.wireOp",EDGE,"E15.left");var subQ1=sQuery(id+"F0.wireOp",EDGE,"E0");var subQ2=makeQuery(id+"F0.imprint","INTERSECT",VERTEX,{"disambiguationData":[OD(0.0)],"derivedFrom":[subQ1,subQ0]});Q85=makeQuery(id+"F0.imprint","IMPRINT",FACE,{"disambiguationData":[TD([[makeQuery(id+"F0.imprint","IMPRINT",EDGE,{"disambiguationData":[TD([[subQ2,-1.0]])],"derivedFrom":subQ1}),1.0]])]});}
            var Q86;
            {var subQ0=sQuery(id+"F0.wireOp",EDGE,"E16.top");var subQ1=sQuery(id+"F0.wireOp",EDGE,"E0");var subQ2=makeQuery(id+"F0.imprint","INTERSECT",VERTEX,{"disambiguationData":[OD(0.0)],"derivedFrom":[subQ1,subQ0]});Q86=makeQuery(id+"F0.imprint","IMPRINT",FACE,{"disambiguationData":[TD([[makeQuery(id+"F0.imprint","IMPRINT",EDGE,{"disambiguationData":[TD([[subQ2,1.0]])],"derivedFrom":subQ1}),1.0]])]});}
            var Q87;
            {var subQ0=sQuery(id+"F0.wireOp",EDGE,"E15.right");var subQ1=sQuery(id+"F0.wireOp",EDGE,"E0");var subQ2=makeQuery(id+"F0.imprint","INTERSECT",VERTEX,{"disambiguationData":[OD(1.0)],"derivedFrom":[subQ1,subQ0]});Q87=makeQuery(id+"F0.imprint","IMPRINT",FACE,{"disambiguationData":[TD([[makeQuery(id+"F0.imprint","IMPRINT",EDGE,{"disambiguationData":[TD([[subQ2,-1.0]])],"derivedFrom":subQ1}),1.0]])]});}
            var Q88;
            {var subQ0=sQuery(id+"F0.wireOp",EDGE,"E16.top");var subQ1=sQuery(id+"F0.wireOp",EDGE,"E0");var subQ2=makeQuery(id+"F0.imprint","INTERSECT",VERTEX,{"disambiguationData":[OD(1.0)],"derivedFrom":[subQ1,subQ0]});Q88=makeQuery(id+"F0.imprint","IMPRINT",FACE,{"disambiguationData":[TD([[makeQuery(id+"F0.imprint","IMPRINT",EDGE,{"disambiguationData":[TD([[subQ2,-1.0]])],"derivedFrom":subQ1}),-1.0]])]});}
            var Q89;
            {var subQ5=sQuery(id+"F0.wireOp",EDGE,"E16.left");Q89=makeQuery(id+"F0.imprint","IMPRINT",FACE,{"disambiguationData":[TD([[makeQuery(id+"F0.imprint","IMPRINT",EDGE,{"derivedFrom":subQ5}),-1.0]])]});}
            var Q90;
            {var subQ0=sQuery(id+"F0.wireOp",EDGE,"E16.top");var subQ1=sQuery(id+"F0.wireOp",EDGE,"E0");var subQ2=makeQuery(id+"F0.imprint","INTERSECT",VERTEX,{"disambiguationData":[OD(0.0)],"derivedFrom":[subQ1,subQ0]});Q90=makeQuery(id+"F0.imprint","IMPRINT",FACE,{"disambiguationData":[TD([[makeQuery(id+"F0.imprint","IMPRINT",EDGE,{"disambiguationData":[TD([[subQ2,1.0]])],"derivedFrom":subQ1}),-1.0]])]});}
            var Q91;
            {var subQ5=sQuery(id+"F0.wireOp",EDGE,"E16.right");Q91=makeQuery(id+"F0.imprint","IMPRINT",FACE,{"disambiguationData":[TD([[makeQuery(id+"F0.imprint","IMPRINT",EDGE,{"derivedFrom":subQ5}),1.0]])]});}
            extrude(context, id + "F1", {"entities" : qUnion([Q0, Q1, Q2, Q3, Q4, Q5, Q6, Q7, Q8, Q9, Q10, Q11, Q12, Q13, Q14, Q15, Q16, Q17, Q18, Q19, Q20, Q21, Q22, Q23, Q24, Q25, Q26, Q27, Q28, Q29, Q30, Q31, Q32, Q33, Q34, Q35, Q36, Q37, Q38, Q39, Q40, Q41, Q42, Q43, Q44, Q45, Q46, Q47, Q48, Q49, Q50, Q51, Q52, Q53, Q54, Q55, Q56, Q57, Q58, Q59, Q60, Q61, Q62, Q63, Q64, Q65, Q66, Q67, Q68, Q69, Q70, Q71, Q72, Q73, Q74, Q75, Q76, Q77, Q78, Q79, Q80, Q81, Q82, Q83, Q84, Q85, Q86, Q87, Q88, Q89, Q90, Q91]), "depth" : 5 * mm, "offsetDistance" : 25 * mm});
        }
    });
